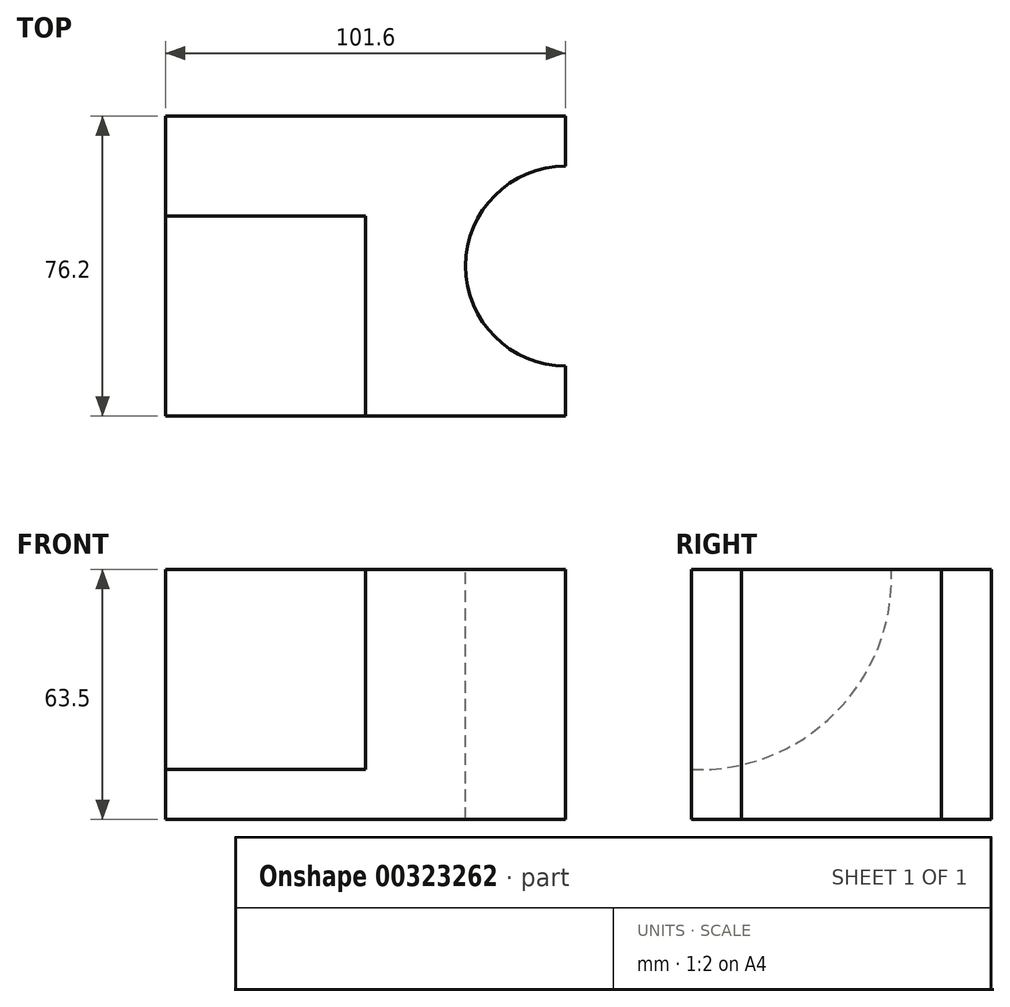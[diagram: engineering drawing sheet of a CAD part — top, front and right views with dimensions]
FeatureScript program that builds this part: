
annotation { "Feature Type Name" : "Feature", "Feature Type Description" : "" }
export const myFeature = defineFeature(function(context is Context, id is Id, definition is map)
    precondition{}
    {
        {
            var Q0;
            Q0=qCreatedBy(makeId("Front.planeOp"),FACE);
            var sketch = newSketch(context, id + "F0", { "sketchPlane" : qUnion([Q0])});
            skLineSegment(sketch, "E0.bottom", {"start": v(-47.33, 14.32) * mm, "end": v(54.27, 14.32) * mm});
            skLineSegment(sketch, "E0.top", {"start": v(-47.33, -49.18) * mm, "end": v(54.27, -49.18) * mm});
            skLineSegment(sketch, "E0.left", {"start": v(-47.33, 14.32) * mm, "end": v(-47.33, -49.18) * mm});
            skLineSegment(sketch, "E0.right", {"start": v(54.27, 14.32) * mm, "end": v(54.27, -49.18) * mm});
            skSolve(sketch);
        }
        {
            var Q0;
            Q0=makeQuery(id+"F0.imprint","IMPRINT",FACE,{"disambiguationData":[TD([[makeQuery(id+"F0.imprint","IMPRINT",EDGE,{"derivedFrom":sQuery(id+"F0.wireOp",EDGE,"E0.bottom")}),-1.0]])]});
            extrude(context, id + "F1", {"entities" : qUnion([Q0]), "depth" : 76.2 * mm});
        }
        {
            var Q0;
            Q0=makeQuery(id+"F1.opExtrude","SWEPT_FACE",FACE,{"disambiguationData":[OSD([sQuery(id+"F0.wireOp",EDGE,"E0.bottom")])]});
            var sketch = newSketch(context, id + "F2", { "sketchPlane" : qUnion([Q0])});
            skLineSegment(sketch, "E1", {"start": v(54.27, 0) * mm, "end": v(54.27, -76.2) * mm});
            skArc(sketch, "E2", {"start": v(54.27, -12.7) * mm, "mid": v(28.87, -38.1) * mm, "end": v(54.27, -63.5) * mm});
            skSolve(sketch);
        }
        {
            var Q0;
            {var subQ0=sQuery(id+"F2.wireOp",EDGE,"E2");Q0=makeQuery(id+"F2.imprint","IMPRINT",FACE,{"disambiguationData":[TD([[makeQuery(id+"F2.imprint","IMPRINT",EDGE,{"derivedFrom":subQ0}),1.0]])]});}
            extrude(context, id + "F3", {"entities" : qUnion([Q0]), "operationType" : NewBodyOperationType.REMOVE, "oppositeDirection" : true, "depth" : 63.5 * mm});
        }
        {
            var Q0;
            Q0=makeQuery(id+"F1.opExtrude","SWEPT_FACE",FACE,{"disambiguationData":[OSD([sQuery(id+"F0.wireOp",EDGE,"E0.left")])]});
            var sketch = newSketch(context, id + "F4", { "sketchPlane" : qUnion([Q0])});
            skCircle(sketch, "E3", {"center": v(76.2, 14.32) * mm, "radius": 53.79 * mm});
            skSolve(sketch);
        }
        {
            var Q0;
            {var subQ0=sQuery(id+"F4.wireOp",EDGE,"E3");var subQ1=sQuery(id+"F0.wireOp",EDGE,"E0.left");var subQ4=makeQuery(id+"F1.opExtrude","CAP_EDGE",EDGE,{"disambiguationData":[OSD([subQ1])],"isStart":false});var subQ5=makeQuery(id+"F4.imprint","INTERSECT",VERTEX,{"derivedFrom":[subQ4,subQ0]});Q0=makeQuery(id+"F4.imprint","IMPRINT",FACE,{"disambiguationData":[TD([[makeQuery(id+"F4.imprint","IMPRINT",EDGE,{"disambiguationData":[TD([[subQ5,-1.0]])],"derivedFrom":subQ0}),1.0]])]});}
            extrude(context, id + "F5", {"entities" : qUnion([Q0]), "operationType" : NewBodyOperationType.REMOVE, "oppositeDirection" : true, "depth" : 50.8 * mm});
        }
        {
            var Q0;
            Q0=makeQuery(id+"F1.opExtrude","SWEPT_FACE",FACE,{"disambiguationData":[OSD([sQuery(id+"F0.wireOp",EDGE,"E0.left")])]});
            var sketch = newSketch(context, id + "F6", { "sketchPlane" : qUnion([Q0])});
            skArc(sketch, "E4", {"start": v(25.4, 14.32) * mm, "mid": v(39.7, -22.19) * mm, "end": v(76.2, -36.48) * mm});
            skSolve(sketch);
        }
        {
            var Q0;
            Q0 = qSketchRegion(id + "F6", true);
            var Q1;
            {var subQ0=sQuery(id+"F6.wireOp",EDGE,"E4");Q1=makeQuery(id+"F6.imprint","IMPRINT",FACE,{"disambiguationData":[TD([[makeQuery(id+"F6.imprint","IMPRINT",EDGE,{"derivedFrom":subQ0}),1.0]])]});}
            extrude(context, id + "F7", {"entities" : qUnion([Q0, Q1]), "operationType" : NewBodyOperationType.REMOVE, "oppositeDirection" : true, "depth" : 50.8 * mm});
        }
    });
